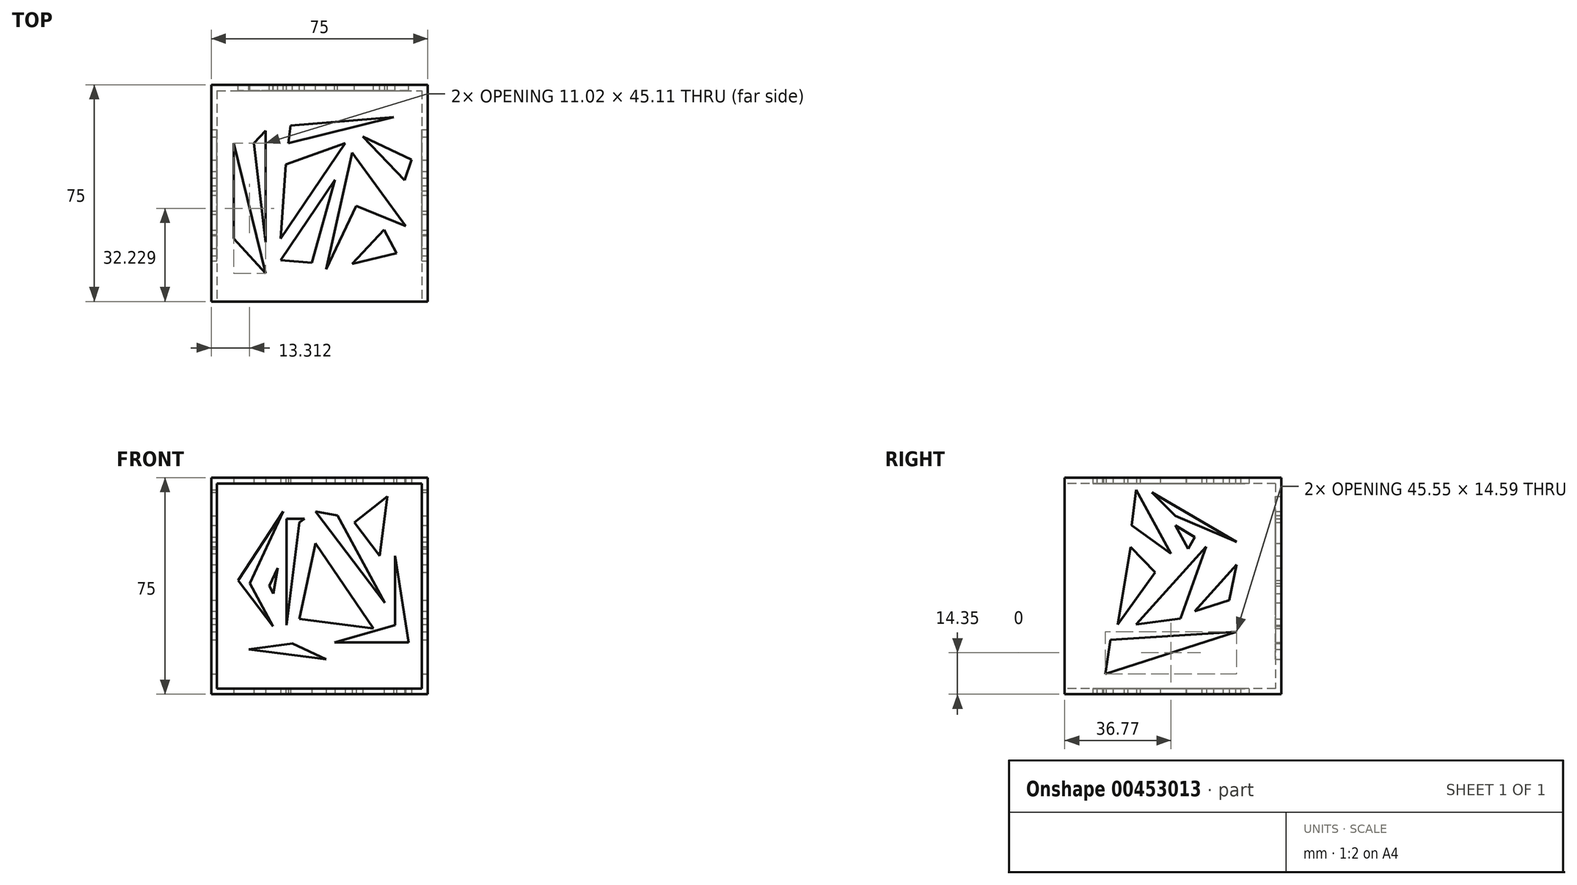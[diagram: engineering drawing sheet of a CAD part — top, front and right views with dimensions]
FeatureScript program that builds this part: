
annotation { "Feature Type Name" : "Feature", "Feature Type Description" : "" }
export const myFeature = defineFeature(function(context is Context, id is Id, definition is map)
    precondition{}
    {
        {
            var Q0;
            Q0=qCreatedBy(makeId("Front.planeOp"),FACE);
            var sketch = newSketch(context, id + "F0", { "sketchPlane" : qUnion([Q0])});
            skLineSegment(sketch, "E0.bottom", {"start": v(-39.8, 39.66) * mm, "end": v(35.2, 39.66) * mm});
            skLineSegment(sketch, "E0.top", {"start": v(-39.8, -35.34) * mm, "end": v(35.2, -35.34) * mm});
            skLineSegment(sketch, "E0.left", {"start": v(-39.8, 39.66) * mm, "end": v(-39.8, -35.34) * mm});
            skLineSegment(sketch, "E0.right", {"start": v(35.2, 39.66) * mm, "end": v(35.2, -35.34) * mm});
            skSolve(sketch);
        }
        {
            var Q0;
            Q0 = qSketchRegion(id + "F0", true);
            extrude(context, id + "F1", {"entities" : qUnion([Q0]), "oppositeDirection" : true, "depth" : 75 * mm});
        }
        {
            var Q0;
            Q0=makeQuery(id+"F1.opExtrude","CAP_FACE",FACE,{"disambiguationData":[OSD([sQuery(id+"F0.wireOp",EDGE,"E0.bottom"),sQuery(id+"F0.wireOp",EDGE,"E0.top"),sQuery(id+"F0.wireOp",EDGE,"E0.left"),sQuery(id+"F0.wireOp",EDGE,"E0.right")])],"isStart":true});
            shell(context, id + "F2", {"entities" : qUnion([Q0]), "thickness" : 2 * mm});
        }
        {
            var Q0;
            Q0=makeQuery(id+"F1.opExtrude","SWEPT_FACE",FACE,{"disambiguationData":[OSD([sQuery(id+"F0.wireOp",EDGE,"E0.top")])]});
            var sketch = newSketch(context, id + "F3", { "sketchPlane" : qUnion([Q0])});
            skLineSegment(sketch, "E1", {"start": v(-25, -54.78) * mm, "end": v(-21, -20.54) * mm});
            skLineSegment(sketch, "E2", {"start": v(-21, -20.54) * mm, "end": v(-21, -59.1) * mm});
            skLineSegment(sketch, "E3", {"start": v(-21, -59.1) * mm, "end": v(-25, -54.78) * mm});
            skLineSegment(sketch, "E4", {"start": v(-15.78, -21.73) * mm, "end": v(6.55, -54.78) * mm});
            skLineSegment(sketch, "E5", {"start": v(6.55, -54.78) * mm, "end": v(-14, -47.49) * mm});
            skLineSegment(sketch, "E6", {"start": v(-14, -47.49) * mm, "end": v(-15.78, -21.73) * mm});
            skLineSegment(sketch, "E7", {"start": v(0, -11.16) * mm, "end": v(9.08, -51.5) * mm});
            skLineSegment(sketch, "E8", {"start": v(9.08, -51.5) * mm, "end": v(27.54, -26.05) * mm});
            skLineSegment(sketch, "E9", {"start": v(27.54, -26.05) * mm, "end": v(10.42, -33.05) * mm});
            skLineSegment(sketch, "E10", {"start": v(10.42, -33.05) * mm, "end": v(0, -11.16) * mm});
            skLineSegment(sketch, "E11", {"start": v(-13.1, -54.78) * mm, "end": v(23.37, -63.86) * mm});
            skLineSegment(sketch, "E12", {"start": v(23.37, -63.86) * mm, "end": v(-12.36, -60.89) * mm});
            skLineSegment(sketch, "E13", {"start": v(-12.36, -60.89) * mm, "end": v(-13.1, -54.78) * mm});
            skLineSegment(sketch, "E14", {"start": v(-15.78, -14.3) * mm, "end": v(2.99, -42.07) * mm});
            skLineSegment(sketch, "E15", {"start": v(2.99, -42.07) * mm, "end": v(-4.91, -13.4) * mm});
            skLineSegment(sketch, "E16", {"start": v(-4.91, -13.4) * mm, "end": v(-15.78, -14.3) * mm});
            skLineSegment(sketch, "E17", {"start": v(-21, -9.68) * mm, "end": v(-32, -54.78) * mm});
            skLineSegment(sketch, "E18", {"start": v(-32, -54.78) * mm, "end": v(-32, -21.73) * mm});
            skLineSegment(sketch, "E19", {"start": v(-32, -21.73) * mm, "end": v(-21, -9.68) * mm});
            skLineSegment(sketch, "E20", {"start": v(27.22, -41.97) * mm, "end": v(12.76, -57.04) * mm});
            skLineSegment(sketch, "E21", {"start": v(12.76, -57.04) * mm, "end": v(29.55, -49.04) * mm});
            skLineSegment(sketch, "E22", {"start": v(29.55, -49.04) * mm, "end": v(27.22, -41.97) * mm});
            skLineSegment(sketch, "E23", {"start": v(9.08, -13.03) * mm, "end": v(20.07, -24.84) * mm});
            skLineSegment(sketch, "E24", {"start": v(20.07, -24.84) * mm, "end": v(24.4, -16.75) * mm});
            skLineSegment(sketch, "E25", {"start": v(24.4, -16.75) * mm, "end": v(9.08, -13.03) * mm});
            skSolve(sketch);
        }
        {
            var Q0;
            Q0 = qSketchRegion(id + "F3", true);
            extrude(context, id + "F4", {"entities" : qUnion([Q0]), "operationType" : NewBodyOperationType.REMOVE, "oppositeDirection" : true, "depth" : 146.3 * mm});
        }
        {
            var Q0;
            Q0=makeQuery(id+"F1.opExtrude","SWEPT_FACE",FACE,{"disambiguationData":[OSD([sQuery(id+"F0.wireOp",EDGE,"E0.right")])]});
            var sketch = newSketch(context, id + "F5", { "sketchPlane" : qUnion([Q0])});
            skLineSegment(sketch, "E26", {"start": v(14, -28.28) * mm, "end": v(59.55, -13.7) * mm});
            skLineSegment(sketch, "E27", {"start": v(59.55, -13.7) * mm, "end": v(15.84, -16.52) * mm});
            skLineSegment(sketch, "E28", {"start": v(15.84, -16.52) * mm, "end": v(14, -28.28) * mm});
            skLineSegment(sketch, "E29", {"start": v(18.37, -11.17) * mm, "end": v(31.3, 6.82) * mm});
            skLineSegment(sketch, "E30", {"start": v(31.3, 6.82) * mm, "end": v(22.83, 15.59) * mm});
            skLineSegment(sketch, "E31", {"start": v(22.83, 15.59) * mm, "end": v(18.37, -11.17) * mm});
            skLineSegment(sketch, "E32", {"start": v(24.76, -11.17) * mm, "end": v(49, 15.74) * mm});
            skLineSegment(sketch, "E33", {"start": v(49, 15.74) * mm, "end": v(40.07, -9.09) * mm});
            skLineSegment(sketch, "E34", {"start": v(40.07, -9.09) * mm, "end": v(24.76, -11.17) * mm});
            skLineSegment(sketch, "E35", {"start": v(23.23, 23.15) * mm, "end": v(36.83, 13.37) * mm});
            skLineSegment(sketch, "E36", {"start": v(36.83, 13.37) * mm, "end": v(24.76, 35.43) * mm});
            skLineSegment(sketch, "E37", {"start": v(24.76, 35.43) * mm, "end": v(23.23, 23.15) * mm});
            skLineSegment(sketch, "E38", {"start": v(38.28, 26.44) * mm, "end": v(59.55, 17.44) * mm});
            skLineSegment(sketch, "E39", {"start": v(59.55, 17.44) * mm, "end": v(30.15, 34.57) * mm});
            skLineSegment(sketch, "E40", {"start": v(30.15, 34.57) * mm, "end": v(38.28, 26.44) * mm});
            skLineSegment(sketch, "E41", {"start": v(45.02, -6.6) * mm, "end": v(59.55, 9.52) * mm});
            skLineSegment(sketch, "E42", {"start": v(59.55, 9.52) * mm, "end": v(56.96, -2.8) * mm});
            skLineSegment(sketch, "E43", {"start": v(56.96, -2.8) * mm, "end": v(45.02, -6.6) * mm});
            skLineSegment(sketch, "E44", {"start": v(38.28, 23.15) * mm, "end": v(42.7, 15.05) * mm});
            skLineSegment(sketch, "E45", {"start": v(42.7, 15.05) * mm, "end": v(45.02, 19.04) * mm});
            skLineSegment(sketch, "E46", {"start": v(45.02, 19.04) * mm, "end": v(38.28, 23.15) * mm});
            skSolve(sketch);
        }
        {
            var Q0;
            Q0 = qSketchRegion(id + "F5", true);
            extrude(context, id + "F6", {"entities" : qUnion([Q0]), "operationType" : NewBodyOperationType.REMOVE, "oppositeDirection" : true, "depth" : 84.9 * mm});
        }
        {
            var Q0;
            Q0=makeQuery(id+"F1.opExtrude","CAP_FACE",FACE,{"disambiguationData":[OSD([sQuery(id+"F0.wireOp",EDGE,"E0.bottom"),sQuery(id+"F0.wireOp",EDGE,"E0.top"),sQuery(id+"F0.wireOp",EDGE,"E0.left"),sQuery(id+"F0.wireOp",EDGE,"E0.right")])],"isStart":false});
            var sketch = newSketch(context, id + "F7", { "sketchPlane" : qUnion([Q0])});
            skLineSegment(sketch, "E47", {"start": v(3.7, 27.97) * mm, "end": v(-20.3, -3.73) * mm});
            skLineSegment(sketch, "E48", {"start": v(-20.3, -3.73) * mm, "end": v(-4, 26.54) * mm});
            skLineSegment(sketch, "E49", {"start": v(-4, 26.54) * mm, "end": v(3.7, 27.97) * mm});
            skLineSegment(sketch, "E50", {"start": v(9.25, 24.2) * mm, "end": v(13.73, -11.43) * mm});
            skLineSegment(sketch, "E51", {"start": v(13.73, -11.43) * mm, "end": v(13.73, 25.46) * mm});
            skLineSegment(sketch, "E52", {"start": v(13.73, 25.46) * mm, "end": v(7.46, 25.46) * mm});
            skLineSegment(sketch, "E53", {"start": v(7.46, 25.46) * mm, "end": v(9.25, 24.2) * mm});
            skLineSegment(sketch, "E54", {"start": v(3.7, 16.87) * mm, "end": v(-16.36, -12.5) * mm});
            skLineSegment(sketch, "E55", {"start": v(-16.36, -12.5) * mm, "end": v(9.25, -9.29) * mm});
            skLineSegment(sketch, "E56", {"start": v(9.25, -9.29) * mm, "end": v(3.7, 16.87) * mm});
            skLineSegment(sketch, "E57", {"start": v(-23.88, 12.57) * mm, "end": v(-23.88, -11.43) * mm});
            skLineSegment(sketch, "E58", {"start": v(-23.88, -11.43) * mm, "end": v(-2.93, -17.34) * mm});
            skLineSegment(sketch, "E59", {"start": v(-2.93, -17.34) * mm, "end": v(-28.53, -17.34) * mm});
            skLineSegment(sketch, "E60", {"start": v(-28.53, -17.34) * mm, "end": v(-23.88, 12.57) * mm});
            skLineSegment(sketch, "E61", {"start": v(14.8, 27.97) * mm, "end": v(26.45, 3.08) * mm});
            skLineSegment(sketch, "E62", {"start": v(26.45, 3.08) * mm, "end": v(18.45, -11.78) * mm});
            skLineSegment(sketch, "E63", {"start": v(18.45, -11.78) * mm, "end": v(30.44, 4.06) * mm});
            skLineSegment(sketch, "E64", {"start": v(30.44, 4.06) * mm, "end": v(14.8, 27.97) * mm});
            skLineSegment(sketch, "E65", {"start": v(16.77, 8.45) * mm, "end": v(19.68, 2.23) * mm});
            skLineSegment(sketch, "E66", {"start": v(19.68, 2.23) * mm, "end": v(18.23, -0.46) * mm});
            skPoint(sketch, "E66.endSnap0", {"position": v(18.23, 5.34) * mm});
            skLineSegment(sketch, "E67", {"start": v(18.23, -0.46) * mm, "end": v(16.77, 8.45) * mm});
            skLineSegment(sketch, "E68", {"start": v(26.8, -19.85) * mm, "end": v(0, -23.22) * mm});
            skLineSegment(sketch, "E69", {"start": v(0, -23.22) * mm, "end": v(11.63, -17.78) * mm});
            skLineSegment(sketch, "E70", {"start": v(11.63, -17.78) * mm, "end": v(26.8, -19.85) * mm});
            skLineSegment(sketch, "E71", {"start": v(-21.2, 33.16) * mm, "end": v(-18.6, 12.57) * mm});
            skLineSegment(sketch, "E72", {"start": v(-18.6, 12.57) * mm, "end": v(-9.8, 24.2) * mm});
            skLineSegment(sketch, "E73", {"start": v(-9.8, 24.2) * mm, "end": v(-21.2, 33.16) * mm});
            skSolve(sketch);
        }
        {
            var Q0;
            Q0 = qSketchRegion(id + "F7", true);
            extrude(context, id + "F8", {"entities" : qUnion([Q0]), "operationType" : NewBodyOperationType.REMOVE, "oppositeDirection" : true, "depth" : 25 * mm});
        }
    });
